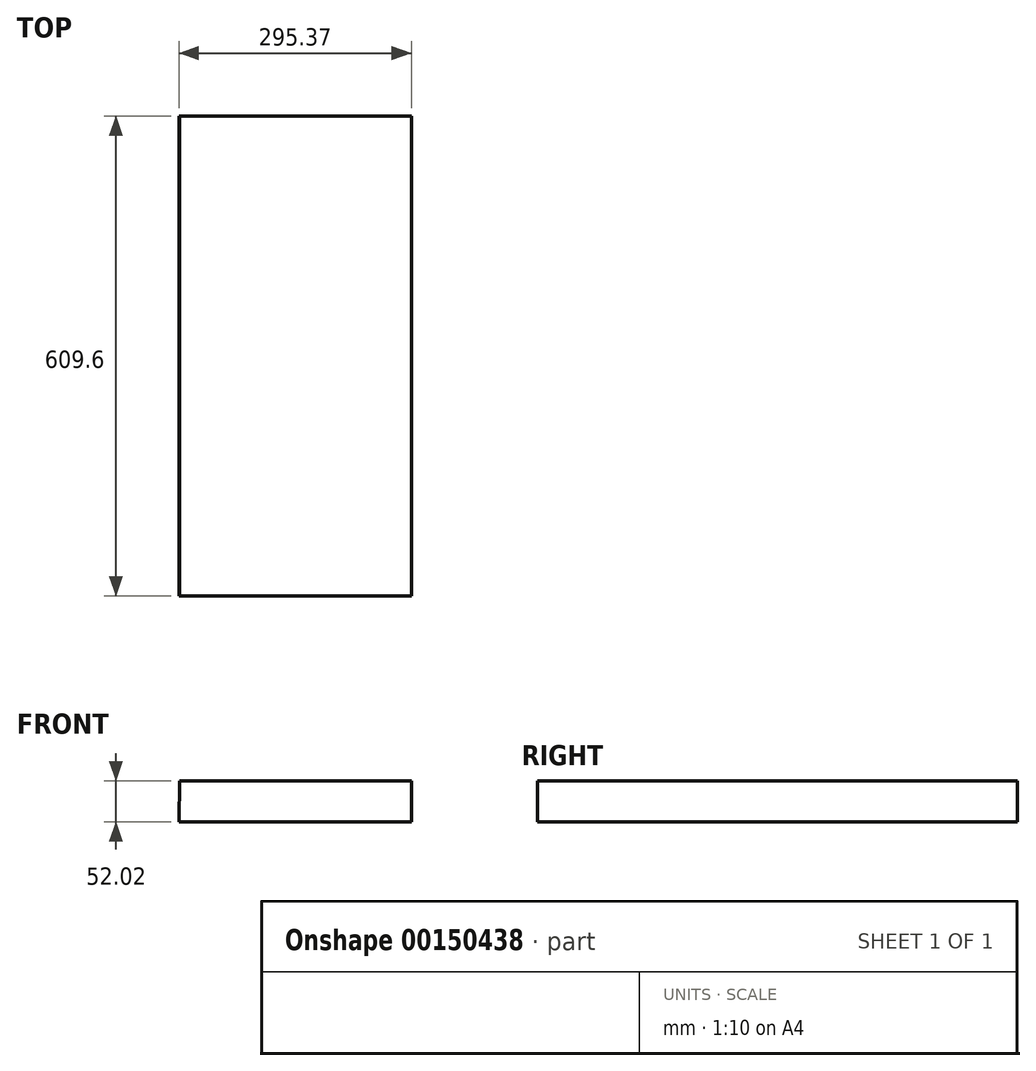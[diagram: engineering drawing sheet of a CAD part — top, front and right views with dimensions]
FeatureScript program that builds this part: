
annotation { "Feature Type Name" : "Feature", "Feature Type Description" : "" }
export const myFeature = defineFeature(function(context is Context, id is Id, definition is map)
    precondition{}
    {
        {
            var Q0;
            Q0=qCreatedBy(makeId("Front.planeOp"), FACE);
            var sketch = newSketch(context, id + "F0", { "sketchPlane" : qUnion([Q0])});
            skLineSegment(sketch, "E0", {"start": v(-144.47, 0) * mm, "end": v(150.26, 0) * mm});
            skLineSegment(sketch, "E1", {"start": v(150.26, 0) * mm, "end": v(150.26, -52.02) * mm});
            skLineSegment(sketch, "E2", {"start": v(150.26, -52.02) * mm, "end": v(-145.11, -52.02) * mm});
            skLineSegment(sketch, "E3", {"start": v(-145.11, -52.02) * mm, "end": v(-144.47, 0) * mm});
            skSolve(sketch);
        }
        {
            var Q0;
            Q0 = qSketchRegion(id + "F0", true);
            extrude(context, id + "F1", {"entities" : qUnion([Q0]), "endBound" : BoundingType.SYMMETRIC, "depth" : 609.6 * mm, "offsetDistance" : 25.4 * mm});
        }
    });
